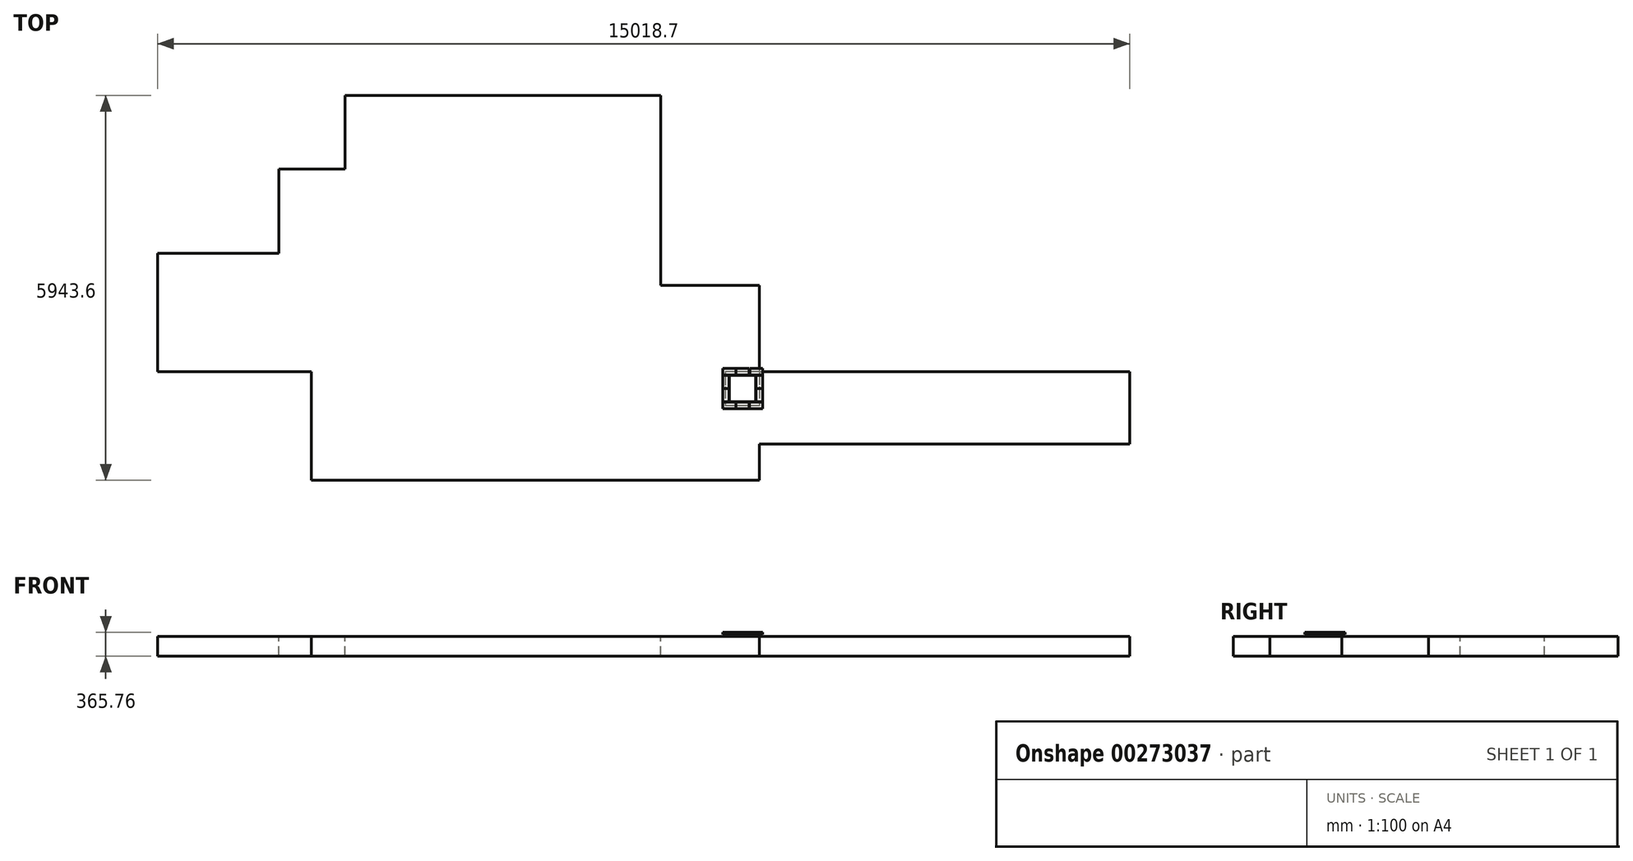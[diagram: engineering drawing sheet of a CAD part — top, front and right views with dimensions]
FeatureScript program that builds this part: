
annotation { "Feature Type Name" : "Feature", "Feature Type Description" : "" }
export const myFeature = defineFeature(function(context is Context, id is Id, definition is map)
    precondition{}
    {
        {
            var Q0;
            Q0=qCreatedBy(makeId("Top.planeOp"),FACE);
            var sketch = newSketch(context, id + "F0", { "sketchPlane" : qUnion([Q0])});
            skLineSegment(sketch, "E0.bottom", {"start": v(-6918.96, 0) * mm, "end": v(0, 0) * mm});
            skLineSegment(sketch, "E0.top", {"start": v(-6918.96, -1676.4) * mm, "end": v(0, -1676.4) * mm});
            skLineSegment(sketch, "E0.left", {"start": v(-6918.96, 0) * mm, "end": v(-6918.96, -1676.4) * mm});
            skLineSegment(sketch, "E0.right", {"start": v(0, 0) * mm, "end": v(0, -1676.4) * mm});
            skLineSegment(sketch, "E1", {"start": v(-1524, 0) * mm, "end": v(-1524, 4267.2) * mm});
            skLineSegment(sketch, "E2", {"start": v(-1524, 4267.2) * mm, "end": v(-6400.8, 4267.2) * mm});
            skLineSegment(sketch, "E3", {"start": v(-6400.8, 4267.2) * mm, "end": v(-6400.8, 3131.77) * mm});
            skLineSegment(sketch, "E4", {"start": v(-6400.8, 3131.77) * mm, "end": v(-7419.45, 3131.77) * mm});
            skLineSegment(sketch, "E5", {"start": v(-7419.45, 3131.77) * mm, "end": v(-7419.45, 1828.8) * mm});
            skLineSegment(sketch, "E6", {"start": v(-7419.45, 1828.8) * mm, "end": v(-9296.4, 1828.8) * mm});
            skLineSegment(sketch, "E7", {"start": v(-9296.4, 1828.8) * mm, "end": v(-9296.4, 0) * mm});
            skLineSegment(sketch, "E8", {"start": v(-9296.4, 0) * mm, "end": v(-6918.96, 0) * mm});
            skLineSegment(sketch, "E9", {"start": v(-1524, 1337.12) * mm, "end": v(0, 1337.12) * mm});
            skLineSegment(sketch, "E10", {"start": v(0, 1337.12) * mm, "end": v(0, 0) * mm});
            skLineSegment(sketch, "E11", {"start": v(0, 0) * mm, "end": v(5722.3, 0) * mm});
            skLineSegment(sketch, "E12", {"start": v(5722.3, 0) * mm, "end": v(5722.3, -1114.44) * mm});
            skLineSegment(sketch, "E13", {"start": v(5722.3, -1114.44) * mm, "end": v(0, -1114.44) * mm});
            skSolve(sketch);
        }
        {
            var Q0;
            Q0 = qSketchRegion(id + "F0", true);
            extrude(context, id + "F1", {"entities" : qUnion([Q0]), "oppositeDirection" : true, "depth" : 304.8 * mm});
        }
        {
            var Q0;
            Q0=qCreatedBy(makeId("Top.planeOp"),FACE);
            var sketch = newSketch(context, id + "F2", { "sketchPlane" : qUnion([Q0])});
            skLineSegment(sketch, "E14.bottom", {"start": v(0, 0) * mm, "end": v(-528.32, 0) * mm});
            skLineSegment(sketch, "E14.top", {"start": v(0, -528.32) * mm, "end": v(-528.32, -528.32) * mm});
            skLineSegment(sketch, "E14.left", {"start": v(0, 0) * mm, "end": v(0, -528.32) * mm});
            skLineSegment(sketch, "E14.right", {"start": v(-528.32, 0) * mm, "end": v(-528.32, -528.32) * mm});
            skSolve(sketch);
        }
        {
            var Q0;
            Q0 = qSketchRegion(id + "F2", true);
            extrude(context, id + "F3", {"entities" : qUnion([Q0]), "depth" : 30.48 * mm});
        }
        {
            var Q0;
            Q0=makeQuery(id+"F3.opExtrude","CAP_FACE",FACE,{"disambiguationData":[OSD([sQuery(id+"F2.wireOp",EDGE,"E14.bottom"),sQuery(id+"F2.wireOp",EDGE,"E14.top"),sQuery(id+"F2.wireOp",EDGE,"E14.left"),sQuery(id+"F2.wireOp",EDGE,"E14.right")])],"isStart":false});
            var sketch = newSketch(context, id + "F4", { "sketchPlane" : qUnion([Q0])});
            skLineSegment(sketch, "E15.bottom", {"start": v(-528.32, 0) * mm, "end": v(-57.91, 0) * mm});
            skLineSegment(sketch, "E15.top", {"start": v(-464.31, -464.31) * mm, "end": v(-57.91, -464.31) * mm});
            skLineSegment(sketch, "E15.right", {"start": v(-57.91, -57.91) * mm, "end": v(-57.91, -464.31) * mm});
            skLineSegment(sketch, "E16", {"start": v(-57.91, -57.91) * mm, "end": v(-464.31, -57.91) * mm});
            skLineSegment(sketch, "E17", {"start": v(-464.31, -57.91) * mm, "end": v(-464.31, -464.31) * mm});
            skSolve(sketch);
        }
        {
            var Q0;
            Q0 = qSketchRegion(id + "F4", true);
            extrude(context, id + "F5", {"entities" : qUnion([Q0]), "operationType" : NewBodyOperationType.ADD, "depth" : 30.48 * mm});
        }
        {
            var Q0;
            Q0=makeQuery(id+"F3.opExtrude","CAP_FACE",FACE,{"disambiguationData":[OSD([sQuery(id+"F2.wireOp",EDGE,"E14.bottom"),sQuery(id+"F2.wireOp",EDGE,"E14.top"),sQuery(id+"F2.wireOp",EDGE,"E14.left"),sQuery(id+"F2.wireOp",EDGE,"E14.right")])],"isStart":false});
            var sketch = newSketch(context, id + "F6", { "sketchPlane" : qUnion([Q0])});
            skLineSegment(sketch, "E18.bottom", {"start": v(49.78, -470.4) * mm, "end": v(-153.42, -470.4) * mm});
            skLineSegment(sketch, "E18.top", {"start": v(49.78, -572) * mm, "end": v(-153.42, -572) * mm});
            skLineSegment(sketch, "E18.right", {"start": v(-153.42, -470.4) * mm, "end": v(-153.42, -572) * mm});
            skLineSegment(sketch, "E19.bottom", {"start": v(-156.46, -572) * mm, "end": v(-359.66, -572) * mm});
            skLineSegment(sketch, "E19.top", {"start": v(-156.46, -470.4) * mm, "end": v(-359.66, -470.4) * mm});
            skLineSegment(sketch, "E19.left", {"start": v(-156.46, -572) * mm, "end": v(-156.46, -470.4) * mm});
            skLineSegment(sketch, "E19.right", {"start": v(-359.66, -572) * mm, "end": v(-359.66, -470.4) * mm});
            skLineSegment(sketch, "E20.0", {"start": v(-464.31, -464.31) * mm, "end": v(-57.91, -464.31) * mm});
            skLineSegment(sketch, "E21.bottom", {"start": v(-51.82, -464.31) * mm, "end": v(49.78, -464.31) * mm});
            skLineSegment(sketch, "E21.top", {"start": v(-51.82, -261.11) * mm, "end": v(49.78, -261.11) * mm});
            skLineSegment(sketch, "E21.left", {"start": v(-51.82, -464.31) * mm, "end": v(-51.82, -261.11) * mm});
            skLineSegment(sketch, "E21.right", {"start": v(49.78, -464.31) * mm, "end": v(49.78, -261.11) * mm});
            skLineSegment(sketch, "E22.bottom", {"start": v(-51.82, -258.06) * mm, "end": v(49.78, -258.06) * mm});
            skLineSegment(sketch, "E22.top", {"start": v(-51.82, -54.86) * mm, "end": v(49.78, -54.86) * mm});
            skLineSegment(sketch, "E22.left", {"start": v(-51.82, -258.06) * mm, "end": v(-51.82, -54.86) * mm});
            skLineSegment(sketch, "E22.right", {"start": v(49.78, -258.06) * mm, "end": v(49.78, -54.86) * mm});
            skLineSegment(sketch, "E23.0", {"start": v(-57.91, -464.31) * mm, "end": v(-57.91, -464.31) * mm});
            skLineSegment(sketch, "E24", {"start": v(49.78, -572) * mm, "end": v(49.78, -470.4) * mm});
            skLineSegment(sketch, "E25.bottom", {"start": v(-362.71, -470.4) * mm, "end": v(-565.91, -470.4) * mm});
            skLineSegment(sketch, "E25.top", {"start": v(-362.71, -572) * mm, "end": v(-565.91, -572) * mm});
            skLineSegment(sketch, "E25.left", {"start": v(-362.71, -470.4) * mm, "end": v(-362.71, -572) * mm});
            skLineSegment(sketch, "E25.right", {"start": v(-565.91, -470.4) * mm, "end": v(-565.91, -572) * mm});
            skLineSegment(sketch, "E26.bottom", {"start": v(-147.32, -51.82) * mm, "end": v(49.78, -51.82) * mm});
            skLineSegment(sketch, "E26.top", {"start": v(-153.42, 49.78) * mm, "end": v(49.78, 49.78) * mm});
            skLineSegment(sketch, "E26.left", {"start": v(-153.42, -45.72) * mm, "end": v(-153.42, 49.78) * mm});
            skLineSegment(sketch, "E26.right", {"start": v(49.78, -51.82) * mm, "end": v(49.78, 49.78) * mm});
            skLineSegment(sketch, "E27.bottom", {"start": v(-156.46, -51.82) * mm, "end": v(-359.66, -51.82) * mm});
            skLineSegment(sketch, "E27.top", {"start": v(-156.46, 49.78) * mm, "end": v(-359.66, 49.78) * mm});
            skLineSegment(sketch, "E27.left", {"start": v(-147.32, -51.82) * mm, "end": v(-147.32, 49.78) * mm});
            skLineSegment(sketch, "E27.right", {"start": v(-359.66, -51.82) * mm, "end": v(-359.66, 49.78) * mm});
            skPoint(sketch, "E28.oppositeSnap0", {"position": v(-464.31, -261.11) * mm});
            skLineSegment(sketch, "E28.bottom", {"start": v(-565.91, -464.31) * mm, "end": v(-470.4, -464.31) * mm});
            skLineSegment(sketch, "E28.top", {"start": v(-565.91, -261.11) * mm, "end": v(-470.4, -261.11) * mm});
            skLineSegment(sketch, "E28.left", {"start": v(-565.91, -464.31) * mm, "end": v(-565.91, -261.11) * mm});
            skLineSegment(sketch, "E28.right", {"start": v(-470.4, -464.31) * mm, "end": v(-470.4, -261.11) * mm});
            skLineSegment(sketch, "E29.bottom", {"start": v(-565.91, -258.06) * mm, "end": v(-470.4, -258.06) * mm});
            skLineSegment(sketch, "E29.top", {"start": v(-565.91, -57.91) * mm, "end": v(-470.4, -57.91) * mm});
            skLineSegment(sketch, "E29.left", {"start": v(-565.91, -258.06) * mm, "end": v(-565.91, -57.91) * mm});
            skLineSegment(sketch, "E29.right", {"start": v(-470.4, -258.06) * mm, "end": v(-470.4, -57.91) * mm});
            skLineSegment(sketch, "E30.bottom", {"start": v(-565.91, -51.82) * mm, "end": v(-362.71, -51.82) * mm});
            skLineSegment(sketch, "E30.top", {"start": v(-565.91, 49.78) * mm, "end": v(-362.71, 49.78) * mm});
            skLineSegment(sketch, "E30.left", {"start": v(-565.91, -51.82) * mm, "end": v(-565.91, 49.78) * mm});
            skLineSegment(sketch, "E30.right", {"start": v(-362.71, -51.82) * mm, "end": v(-362.71, 49.78) * mm});
            skLineSegment(sketch, "E31", {"start": v(-156.46, -51.82) * mm, "end": v(-156.46, 49.78) * mm});
            skSolve(sketch);
        }
        {
            var Q0;
            Q0 = qSketchRegion(id + "F6", true);
            extrude(context, id + "F7", {"entities" : qUnion([Q0]), "depth" : 30.48 * mm});
        }
    });
